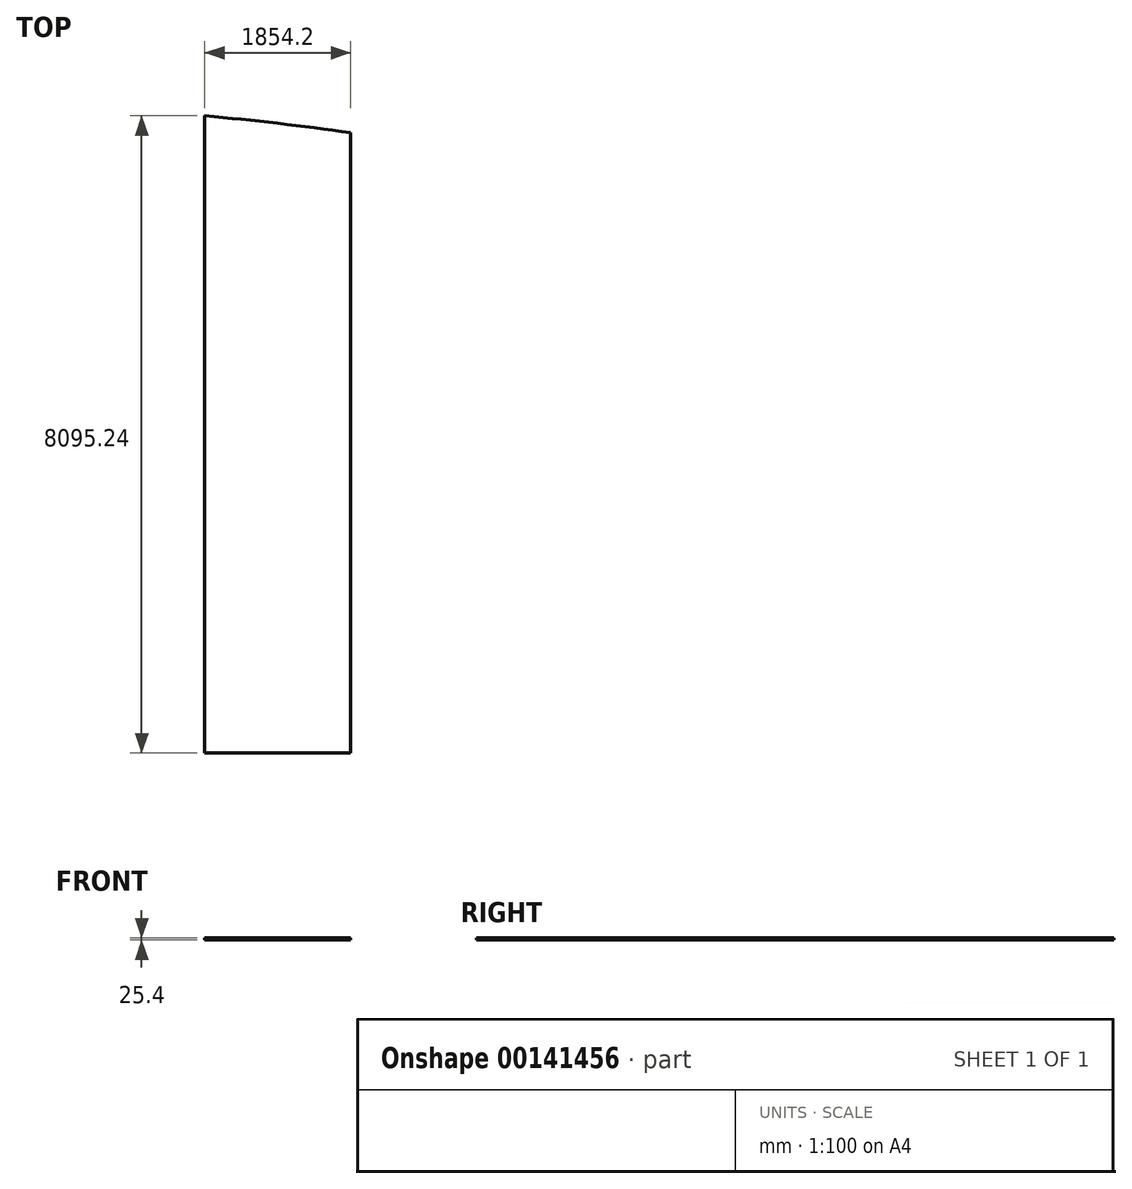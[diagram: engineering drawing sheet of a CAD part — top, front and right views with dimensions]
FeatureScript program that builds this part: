
annotation { "Feature Type Name" : "Feature", "Feature Type Description" : "" }
export const myFeature = defineFeature(function(context is Context, id is Id, definition is map)
    precondition{}
    {
        {
            var Q0;
            Q0=qCreatedBy(makeId("Top.planeOp"),FACE);
            var sketch = newSketch(context, id + "F0", { "sketchPlane" : qUnion([Q0])});
            skLineSegment(sketch, "E0", {"start": v(-966.89, -5975.08) * mm, "end": v(887.31, -5975.08) * mm});
            skLineSegment(sketch, "E1", {"start": v(-966.89, -5975.08) * mm, "end": v(-966.89, 2120.16) * mm});
            skLineSegment(sketch, "E2", {"start": v(887.31, -5975.08) * mm, "end": v(887.31, 1904) * mm});
            skLineSegment(sketch, "E3", {"start": v(-39.79, -5975.08) * mm, "end": v(-39.79, 2024.9) * mm});
            skArc(sketch, "E4", {"start": v(887.31, 1904) * mm, "mid": v(-38.31, 2024.73) * mm, "end": v(-966.89, 2120.16) * mm});
            skSolve(sketch);
        }
        {
            var Q0;
            {var subQ0=sQuery(id+"F0.wireOp",EDGE,"E1");Q0=makeQuery(id+"F0.imprint","IMPRINT",FACE,{"disambiguationData":[TD([[makeQuery(id+"F0.imprint","IMPRINT",EDGE,{"derivedFrom":subQ0}),-1.0]])]});}
            var Q1;
            {var subQ0=sQuery(id+"F0.wireOp",EDGE,"E2");Q1=makeQuery(id+"F0.imprint","IMPRINT",FACE,{"disambiguationData":[TD([[makeQuery(id+"F0.imprint","IMPRINT",EDGE,{"derivedFrom":subQ0}),1.0]])]});}
            extrude(context, id + "F1", {"entities" : qUnion([Q0, Q1]), "depth" : 25.4 * mm});
        }
    });
